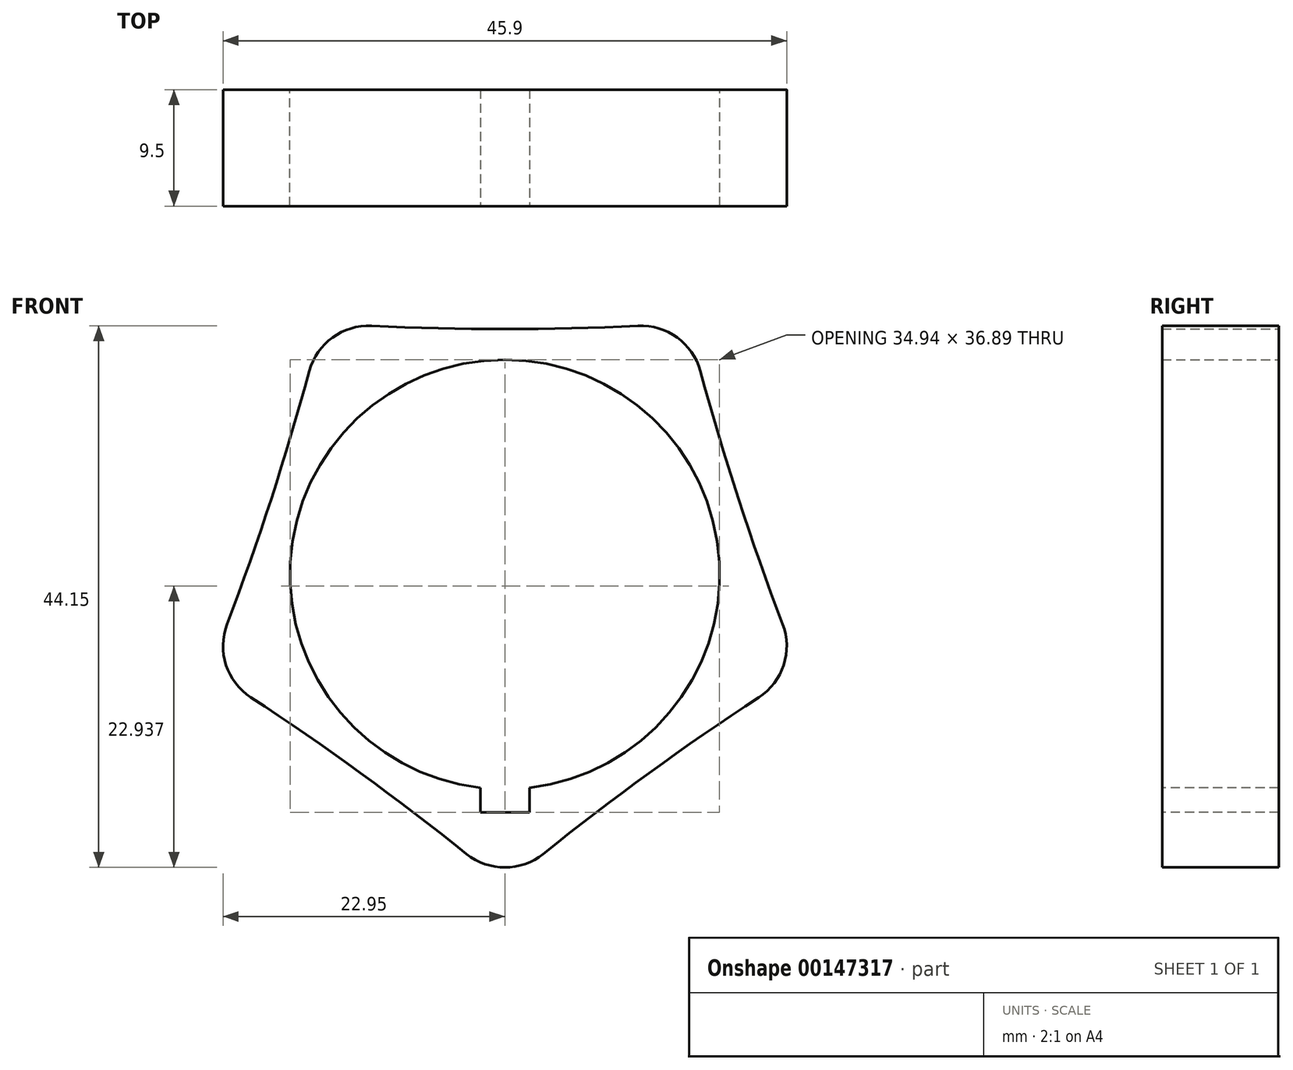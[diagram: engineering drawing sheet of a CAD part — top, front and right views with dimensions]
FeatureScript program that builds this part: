
annotation { "Feature Type Name" : "Feature", "Feature Type Description" : "" }
export const myFeature = defineFeature(function(context is Context, id is Id, definition is map)
    precondition{}
    {
        {
            var Q0;
            Q0=qCreatedBy(makeId("Front.planeOp"),FACE);
            var sketch = newSketch(context, id + "F0", { "sketchPlane" : qUnion([Q0])});
            skCircle(sketch, "E0", {"center": v(0, 0) * mm, "radius": 17.5 * mm});
            skCircle(sketch, "E1.cCircle", {"center": v(0, 0) * mm, "radius": 20 * mm, "construction": true});
            skPoint(sketch, "E1.0.midPoint", {"position": v(0, 20) * mm});
            skLineSegment(sketch, "E2", {"start": v(0, 0) * mm, "end": v(-20.64, 28.41) * mm, "construction": true});
            skLineSegment(sketch, "E3", {"start": v(0, 0) * mm, "end": v(20.64, 28.41) * mm, "construction": true});
            skPoint(sketch, "E4", {"position": v(-14.9, 20.5) * mm});
            skPoint(sketch, "E5.MirrorP", {"position": v(14.9, 20.5) * mm});
            skCircle(sketch, "E6", {"center": v(0, 242.08) * mm, "radius": 222.08 * mm});
            skCircle(sketch, "E7.1.0", {"center": v(-230.24, 74.8) * mm, "radius": 222.08 * mm});
            skCircle(sketch, "E7.2.0", {"center": v(-142.3, -195.85) * mm, "radius": 222.08 * mm});
            skCircle(sketch, "E7.3.0", {"center": v(142.3, -195.85) * mm, "radius": 222.08 * mm});
            skCircle(sketch, "E7.4.0", {"center": v(230.24, 74.8) * mm, "radius": 222.08 * mm});
            skPoint(sketch, "E8", {"position": v(-14.53, 20) * mm});
            skPoint(sketch, "E9", {"position": v(14.53, 20) * mm});
            skPoint(sketch, "E10", {"position": v(-23.51, -7.64) * mm});
            skPoint(sketch, "E11", {"position": v(0, -24.72) * mm});
            skPoint(sketch, "E12", {"position": v(23.51, -7.64) * mm});
            skSolve(sketch);
        }
        {
            var Q0;
            Q0=makeQuery(id+"F0.imprint","IMPRINT",FACE,{"disambiguationData":[TD([[makeQuery(id+"F0.imprint","IMPRINT",EDGE,{"derivedFrom":sQuery(id+"F0.wireOp",EDGE,"E0")}),-1.0]])]});
            extrude(context, id + "F1", {"entities" : qUnion([Q0]), "depth" : 9.5 * mm});
        }
        {
            var Q0;
            Q0=makeQuery(id+"F1.opExtrude","SWEPT_EDGE",EDGE,{"disambiguationData":[OSD([sQuery(id+"F0.wireOp",EDGE,"E7.2.0"),sQuery(id+"F0.wireOp",EDGE,"E7.3.0")])]});
            var Q1;
            Q1=makeQuery(id+"F1.opExtrude","SWEPT_EDGE",EDGE,{"disambiguationData":[OSD([sQuery(id+"F0.wireOp",EDGE,"E7.1.0"),sQuery(id+"F0.wireOp",EDGE,"E7.2.0")])]});
            var Q2;
            Q2=makeQuery(id+"F1.opExtrude","SWEPT_EDGE",EDGE,{"disambiguationData":[OSD([sQuery(id+"F0.wireOp",EDGE,"E6"),sQuery(id+"F0.wireOp",EDGE,"E7.1.0")])]});
            var Q3;
            Q3=makeQuery(id+"F1.opExtrude","SWEPT_EDGE",EDGE,{"disambiguationData":[OSD([sQuery(id+"F0.wireOp",EDGE,"E6"),sQuery(id+"F0.wireOp",EDGE,"E7.4.0")])]});
            var Q4;
            Q4=makeQuery(id+"F1.opExtrude","SWEPT_EDGE",EDGE,{"disambiguationData":[OSD([sQuery(id+"F0.wireOp",EDGE,"E7.3.0"),sQuery(id+"F0.wireOp",EDGE,"E7.4.0")])]});
            fillet(context, id + "F2", {"entities" : qUnion([Q0, Q1, Q2, Q3, Q4]), "radius" : 5 * mm, "tangentPropagation" : true, "allowEdgeOverflow" : false});
        }
        {
            var Q0;
            Q0=makeQuery(id+"F1.opExtrude","CAP_FACE",FACE,{"disambiguationData":[OSD([sQuery(id+"F0.wireOp",EDGE,"E0"),sQuery(id+"F0.wireOp",EDGE,"E6"),sQuery(id+"F0.wireOp",EDGE,"E7.1.0"),sQuery(id+"F0.wireOp",EDGE,"E7.2.0"),sQuery(id+"F0.wireOp",EDGE,"E7.3.0"),sQuery(id+"F0.wireOp",EDGE,"E7.4.0")])],"isStart":false});
            var sketch = newSketch(context, id + "F3", { "sketchPlane" : qUnion([Q0])});
            skLineSegment(sketch, "E13", {"start": v(0, -17.5) * mm, "end": v(0, -20.48) * mm, "construction": true});
            skLineSegment(sketch, "E14", {"start": v(2, -20.48) * mm, "end": v(2, -17.39) * mm, "construction": true});
            skLineSegment(sketch, "E15", {"start": v(2, -17.39) * mm, "end": v(2, -19.39) * mm});
            skLineSegment(sketch, "E16", {"start": v(2, -19.39) * mm, "end": v(0, -19.39) * mm});
            skLineSegment(sketch, "E17.MirrorCS", {"start": v(-2, -19.39) * mm, "end": v(0, -19.39) * mm});
            skLineSegment(sketch, "E18.MirrorCS", {"start": v(-2, -20.48) * mm, "end": v(-2, -17.39) * mm, "construction": true});
            skLineSegment(sketch, "E19", {"start": v(-2, -19.39) * mm, "end": v(-2, -17.39) * mm});
            skLineSegment(sketch, "E20", {"start": v(-2, -17.39) * mm, "end": v(2, -17.39) * mm});
            skSolve(sketch);
        }
        {
            var Q0;
            Q0 = qSketchRegion(id + "F3", true);
            extrude(context, id + "F4", {"entities" : qUnion([Q0]), "operationType" : NewBodyOperationType.REMOVE, "endBound" : BoundingType.THROUGH_ALL, "oppositeDirection" : true, "depth" : 25 * mm});
        }
    });
